# Revit family: Sink-Bradley_Corp-Express-TLX4-Faucet-Soap-WBDuo
name_source: partatom
category: Plumbing Fixtures
units: mm (PartAtom-declared; Revit-internal decimal feet)

## family parameters
Always vertical = Yes
Cut with Voids When Loaded = No
Maintain Annotation Orientation = No
OmniClass Number = 23.45.05.14.14
OmniClass Title = Sinks/Lavatories
Part Type = Normal
Room Calculation Point = No
Round Connector Dimension = Use Diameter
Shared = No
Work Plane-Based = No

## types (2) — shared parameters
ADA Compliant = Yes
Access Panel Material = Metal - Bradley Corp - Stainless Steel
Apparent Load = 0 VA
Assembly Code = D2010400
CWFU = 0.5
Cold Water Connection Diameter = 0.5 "
Cold Water Connection Radius = 0.25 "
Depth = 20.625 "
Description = Express™ Lavatory System – TLX Series, Four-Station
Fixture Material = Metal - Bradley Corp - Chrome
HWFU = 0.5
Height = 34 "
Hot Water Connection Diameter = 0.5 "
Hot Water Connection Radius = 0.25 "
Industry Standards = ANSI Z124.3, ANSI Z124.6, ANSI/OCPA SS-1-2001, UPC, GREENGUARD Indoor Air Quality Certified®, GREENGUARD Children & Schools(SM)
Installation Type = Wall Mounted
Low Emitting Material = Yes
Manufacturer = Bradley Corporation
Manufacturer Installation URL - English = https://www.bradleycorp.com
MasterFormat Number = 22 42 16
MasterFormat Title = Commercial Lavatories and Sinks
Material = Polyester Resin
Material Note = Other Terreon™ colors available - See www.bradleycorp.com
Number of Poles = 1
OmniClass Table 21 Number = 21-04 20 10 60
OmniClass Table 21 Title = Plumbing Fixtures
OmniClass Table 23 Number = 23-31 13 00
OmniClass Table 23 Title = Sink/Lavatories
Pedestal Width = 36 "
Power Factor = 1
Product Page URL = https://www.bradleycorp.com
Product Tech Data URL - English = https://www.bradleycorp.com
Specifications URL = http://www.bradleycorp.com
Terreon™ Bowl Material = Stone - Bradley Corp - Designer White
Trap Cover Material = Plastic - Bradley Corp - Polystyrene - Coal
URL = http://www.bradleycorp.com
Version = 1.0
Voltage = 110 V
WFU = 1.5
Waste Connection Diameter = 1.5 "
Waste Connection Radius = 0.75 "
Width = 85.25 "
zero-valued in all types: Default Elevation, Percentage of Recycled Content

## per-type parameters (varying)
| type | Faucet | Model | Soap Dispenser | WashBar Duo |
| Express TLX-4 Faucet-Soap | Yes | TLX-4 Faucet-Soap Dispenser | Yes | No |
| Express TLX-4 WashBar Duo | No | TLX-4 WashBar Duo | No | Yes |

## geometry (parser evidence)
native form markers: Blend x24, Sweep x10
no freeform markers — native parametric forms only
